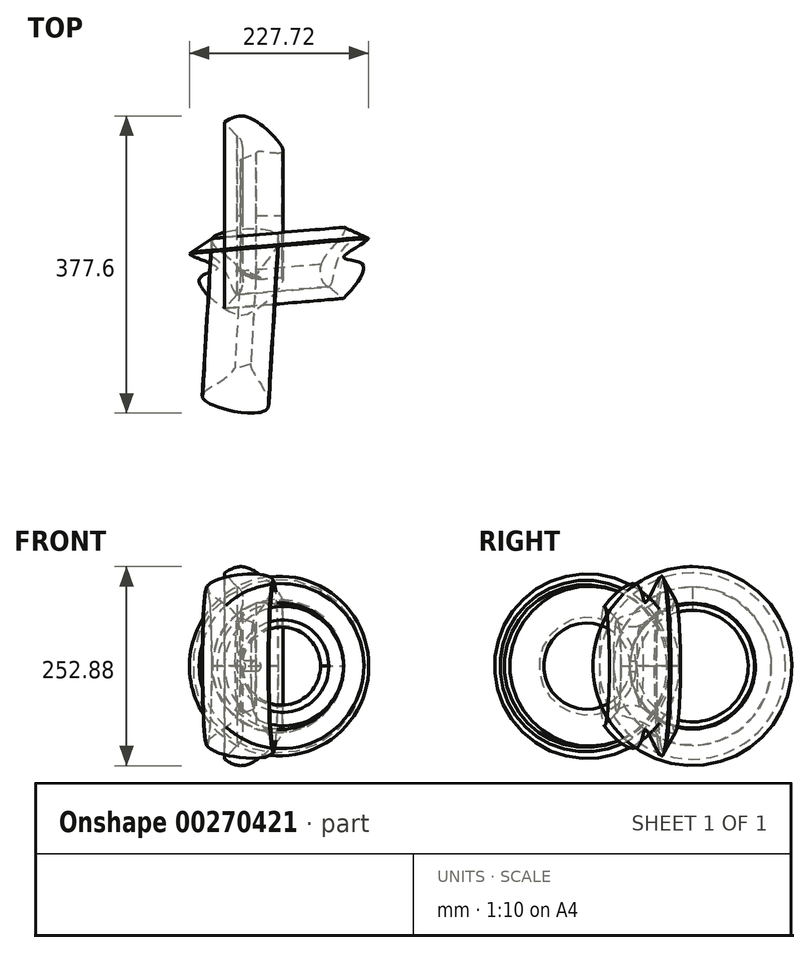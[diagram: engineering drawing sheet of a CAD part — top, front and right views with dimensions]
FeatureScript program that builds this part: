
annotation { "Feature Type Name" : "Feature", "Feature Type Description" : "" }
export const myFeature = defineFeature(function(context is Context, id is Id, definition is map)
    precondition{}
    {
        {
            var Q0;
            Q0=qCreatedBy(makeId("Top.planeOp"),FACE);
            var sketch = newSketch(context, id + "F0", { "sketchPlane" : qUnion([Q0])});
            skFitSpline(sketch, "E0", {"points": [v(0, 0) * mm, v(-36.2, 41.59) * mm, v(47.93, 44.17) * mm, v(19.56, -8.37) * mm, v(52.44, -9.02) * mm, v(16.99, -50.28) * mm, v(-20.4, -47.38) * mm, v(-51.35, -8.37) * mm, v(-29.43, 4.2) * mm, v(-64.89, 22.25) * mm, v(-32.33, 16.45) * mm, v(-4.61, -29.65) * mm, v(0, 0) * mm]});
            skLineSegment(sketch, "E1", {"start": v(-36.2, 41.59) * mm, "end": v(-64.89, 22.25) * mm});
            skLineSegment(sketch, "E2", {"start": v(-4.61, -29.65) * mm, "end": v(-20.4, -47.38) * mm});
            skLineSegment(sketch, "E3", {"start": v(19.56, -8.37) * mm, "end": v(0, 0) * mm});
            skLineSegment(sketch, "E4", {"start": v(52.44, -9.02) * mm, "end": v(47.93, 44.17) * mm});
            skLineSegment(sketch, "E5", {"start": v(67.27, 55.45) * mm, "end": v(70.82, -29.65) * mm});
            skLineSegment(sketch, "E6", {"start": v(70.82, -29.65) * mm, "end": v(44.06, -64.78) * mm});
            skLineSegment(sketch, "E7", {"start": v(44.06, -64.78) * mm, "end": v(-32, -60.27) * mm});
            skLineSegment(sketch, "E8", {"start": v(-32, -60.27) * mm, "end": v(-75.85, -15.14) * mm});
            skLineSegment(sketch, "E9", {"start": v(-75.85, -15.14) * mm, "end": v(-75.85, 58.35) * mm});
            skLineSegment(sketch, "E10", {"start": v(-75.85, 58.35) * mm, "end": v(-20.4, 70.92) * mm});
            skLineSegment(sketch, "E11", {"start": v(-20.4, 70.92) * mm, "end": v(36.33, 70.92) * mm});
            skLineSegment(sketch, "E12", {"start": v(36.33, 70.92) * mm, "end": v(67.27, 55.45) * mm});
            skSolve(sketch);
        }
        {
            var Q0;
            Q0=qCreatedBy(makeId("Front.planeOp"),FACE);
            var sketch = newSketch(context, id + "F1", { "sketchPlane" : qUnion([Q0])});
            skCircle(sketch, "E13", {"center": v(0, 0) * mm, "radius": 6.48 * mm});
            skSolve(sketch);
        }
        {
            var Q0;
            Q0=makeQuery(id+"F1.imprint","IMPRINT",FACE,{"disambiguationData":[TD([[makeQuery(id+"F1.imprint","IMPRINT",EDGE,{"derivedFrom":sQuery(id+"F1.wireOp",EDGE,"E13")}),1.0]])]});
            var Q1;
            Q1=sQuery(id+"F0.wireOp",EDGE,"E3");
            sweep(context, id + "F2", {"profiles" : qUnion([Q0]), "path" : qUnion([Q1])});
        }
        {
            var Q0;
            {var subQ0=sQuery(id+"F0.wireOp",EDGE,"E1");var subQ1=sQuery(id+"F0.wireOp",EDGE,"E0");var subQ2=makeQuery(id+"F0.imprint","INTERSECT",VERTEX,{"disambiguationData":[OD(0.0)],"derivedFrom":[subQ1,subQ0]});Q0=makeQuery(id+"F0.imprint","IMPRINT",FACE,{"disambiguationData":[TD([[makeQuery(id+"F0.imprint","IMPRINT",EDGE,{"disambiguationData":[TD([[subQ2,1.0]])],"derivedFrom":subQ1}),1.0]])]});}
            var Q1;
            Q1=sQuery(id+"F0.wireOp",EDGE,"E4");
            revolve(context, id + "F3", {"entities" : qUnion([Q0]), "axis" : qUnion([Q1]), "revolveType" : RevolveType.FULL});
        }
        {
            var Q0;
            {var subQ3=sQuery(id+"F0.wireOp",EDGE,"E2");Q0=makeQuery(id+"F0.imprint","IMPRINT",FACE,{"disambiguationData":[TD([[makeQuery(id+"F0.imprint","IMPRINT",EDGE,{"derivedFrom":subQ3}),-1.0]])]});}
            var Q1;
            Q1=sQuery(id+"F0.wireOp",EDGE,"E4");
            revolve(context, id + "F4", {"entities" : qUnion([Q0]), "axis" : qUnion([Q1]), "revolveType" : RevolveType.FULL});
        }
        {
            var Q0;
            {var subQ0=sQuery(id+"F0.wireOp",EDGE,"E2");Q0=makeQuery(id+"F0.imprint","IMPRINT",FACE,{"disambiguationData":[TD([[makeQuery(id+"F0.imprint","IMPRINT",EDGE,{"derivedFrom":subQ0}),1.0]])]});}
            var Q1;
            Q1=sQuery(id+"F0.wireOp",EDGE,"E11");
            revolve(context, id + "F5", {"entities" : qUnion([Q0]), "axis" : qUnion([Q1]), "revolveType" : RevolveType.FULL});
        }
        {
            var Q0;
            {var subQ0=sQuery(id+"F0.wireOp",EDGE,"E3");Q0=makeQuery(id+"F0.imprint","IMPRINT",FACE,{"disambiguationData":[TD([[makeQuery(id+"F0.imprint","IMPRINT",EDGE,{"derivedFrom":subQ0}),-1.0]])]});}
            var Q1;
            Q1=sQuery(id+"F0.wireOp",EDGE,"E7");
            revolve(context, id + "F6", {"entities" : qUnion([Q0]), "axis" : qUnion([Q1]), "revolveType" : RevolveType.FULL});
        }
    });
